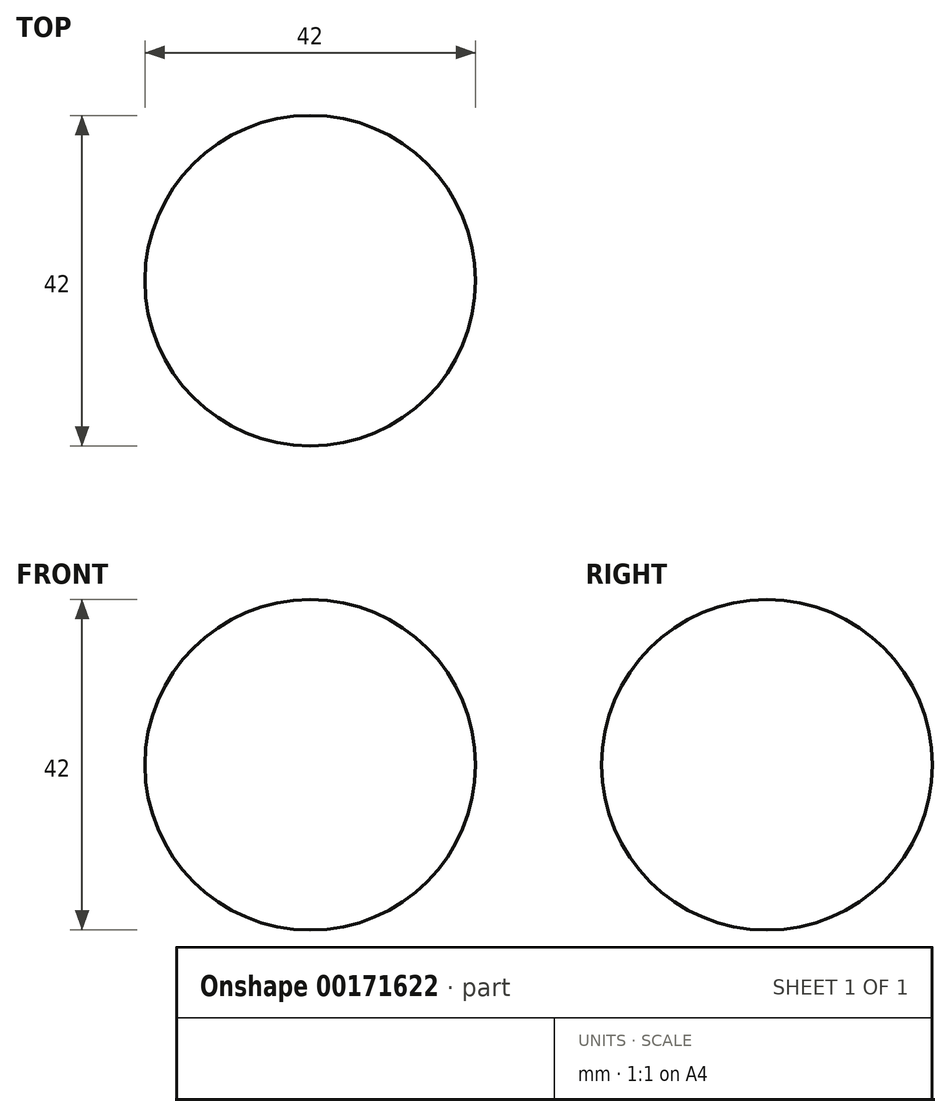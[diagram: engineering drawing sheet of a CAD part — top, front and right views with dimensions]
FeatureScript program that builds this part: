
annotation { "Feature Type Name" : "Feature", "Feature Type Description" : "" }
export const myFeature = defineFeature(function(context is Context, id is Id, definition is map)
    precondition{}
    {
        {
            var Q0;
            Q0=qCreatedBy(makeId("Front.planeOp"),FACE);
            var sketch = newSketch(context, id + "F0", { "sketchPlane" : qUnion([Q0])});
            skArc(sketch, "E0", {"start": v(0, -21) * mm, "mid": v(21, 0) * mm, "end": v(0, 21) * mm});
            skLineSegment(sketch, "E1", {"start": v(0, 21) * mm, "end": v(0, -21) * mm});
            skSolve(sketch);
        }
        {
            var Q0;
            Q0=makeQuery(id+"F0.imprint","IMPRINT",FACE,{"disambiguationData":[TD([[makeQuery(id+"F0.imprint","IMPRINT",EDGE,{"derivedFrom":sQuery(id+"F0.wireOp",EDGE,"E0")}),1.0]])]});
            var Q1;
            Q1=sQuery(id+"F0.wireOp",EDGE,"E1");
            revolve(context, id + "F1", {"entities" : qUnion([Q0]), "axis" : qUnion([Q1]), "revolveType" : RevolveType.FULL});
        }
    });
